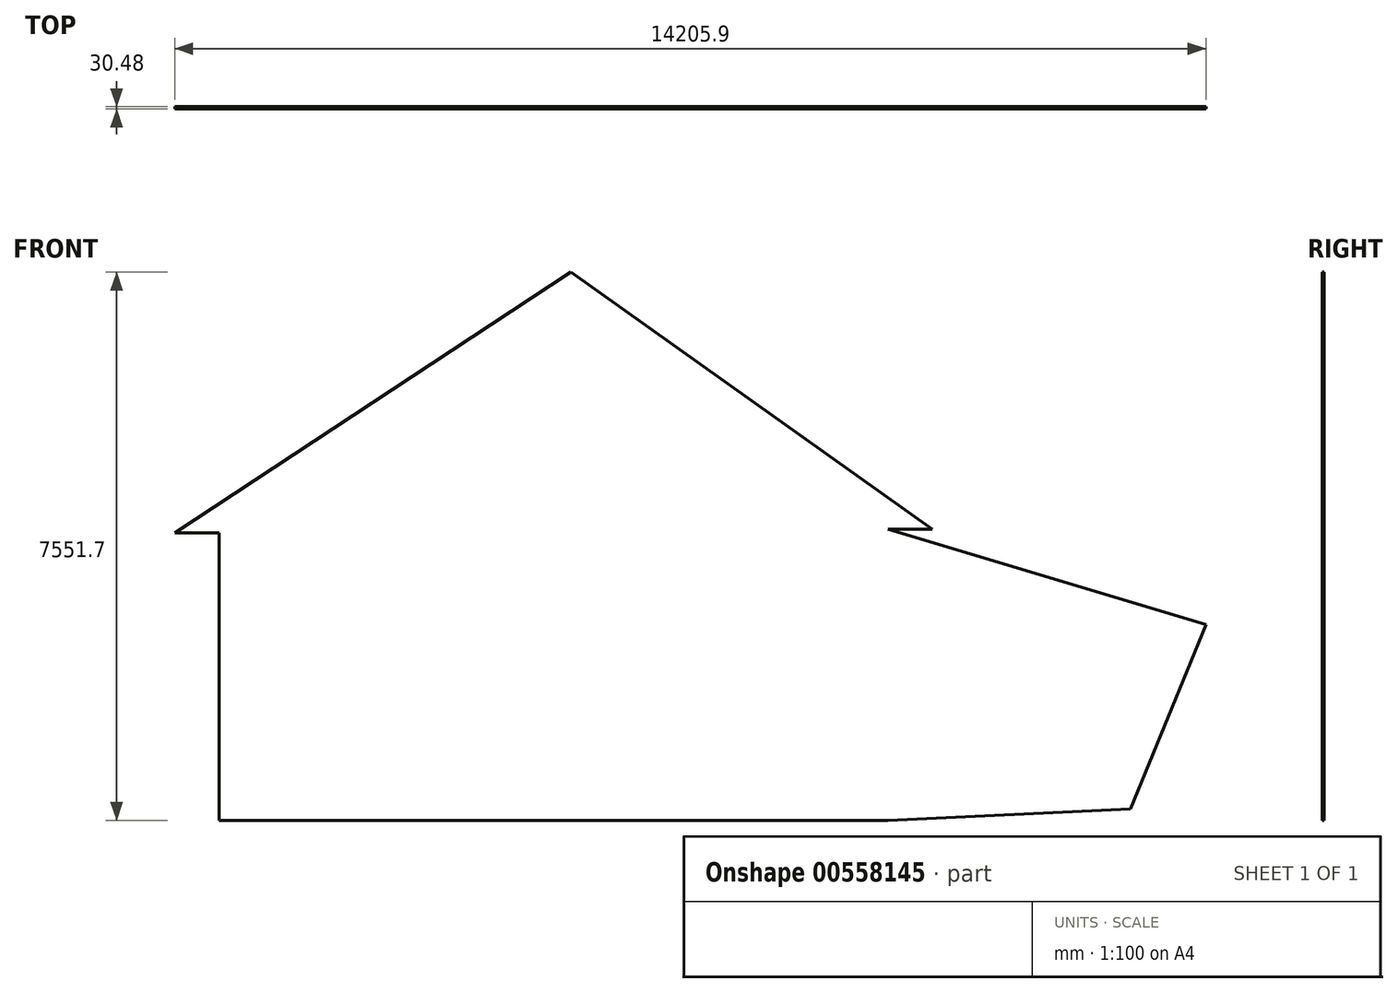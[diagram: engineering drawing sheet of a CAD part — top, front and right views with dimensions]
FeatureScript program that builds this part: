
annotation { "Feature Type Name" : "Feature", "Feature Type Description" : "" }
export const myFeature = defineFeature(function(context is Context, id is Id, definition is map)
    precondition{}
    {
        {
            var Q0;
            Q0=qCreatedBy(makeId("Front.planeOp"),FACE);
            var sketch = newSketch(context, id + "F0", { "sketchPlane" : qUnion([Q0])});
            skLineSegment(sketch, "E0", {"start": v(0, 0) * mm, "end": v(-4572, 0) * mm});
            skLineSegment(sketch, "E1", {"start": v(0, 0) * mm, "end": v(4572, 0) * mm});
            skLineSegment(sketch, "E2", {"start": v(-4572, 0) * mm, "end": v(0, 2750.77) * mm});
            skLineSegment(sketch, "E3", {"start": v(4644.56, 46.62) * mm, "end": v(0, 2750.77) * mm});
            skLineSegment(sketch, "E4", {"start": v(-4572, 0) * mm, "end": v(-4572, -3352.8) * mm});
            skLineSegment(sketch, "E5", {"start": v(4644.56, 46.62) * mm, "end": v(4644.56, -3352.8) * mm});
            skLineSegment(sketch, "E6", {"start": v(4644.56, -3352.8) * mm, "end": v(-4572, -3352.8) * mm});
            skLineSegment(sketch, "E7", {"start": v(-4572, -3352.8) * mm, "end": v(-4572, -3962.4) * mm});
            skLineSegment(sketch, "E8", {"start": v(4644.56, -3352.8) * mm, "end": v(4644.56, -3962.4) * mm});
            skLineSegment(sketch, "E9", {"start": v(-4572, -3962.4) * mm, "end": v(4644.56, -3962.4) * mm});
            skLineSegment(sketch, "E10", {"start": v(-266.42, -1756.14) * mm, "end": v(-266.42, -3352.8) * mm});
            skLineSegment(sketch, "E11", {"start": v(-266.42, -1756.14) * mm, "end": v(821.46, -1756.14) * mm});
            skLineSegment(sketch, "E12", {"start": v(821.46, -1756.14) * mm, "end": v(821.46, -3352.8) * mm});
            skLineSegment(sketch, "E13", {"start": v(-4151.68, -810.66) * mm, "end": v(-4151.68, -1725.06) * mm});
            skLineSegment(sketch, "E14", {"start": v(-4151.68, -1725.06) * mm, "end": v(-2193.5, -1725.06) * mm});
            skLineSegment(sketch, "E15", {"start": v(-2193.5, -1725.06) * mm, "end": v(-2193.5, -854.76) * mm});
            skLineSegment(sketch, "E16", {"start": v(-2193.5, -854.76) * mm, "end": v(-4151.68, -810.66) * mm});
            skLineSegment(sketch, "E17.bottom", {"start": v(1598.5, -1010.17) * mm, "end": v(2748.55, -1010.17) * mm});
            skLineSegment(sketch, "E17.top", {"start": v(1598.5, -1693.97) * mm, "end": v(2748.55, -1693.97) * mm});
            skLineSegment(sketch, "E17.left", {"start": v(1598.5, -1010.17) * mm, "end": v(1598.5, -1693.97) * mm});
            skLineSegment(sketch, "E17.right", {"start": v(2748.55, -1010.17) * mm, "end": v(2748.55, -1693.97) * mm});
            skLineSegment(sketch, "E18", {"start": v(-4572, 0) * mm, "end": v(-5181.6, 0) * mm});
            skLineSegment(sketch, "E19", {"start": v(4644.56, 46.62) * mm, "end": v(5254.16, 46.62) * mm});
            skLineSegment(sketch, "E20", {"start": v(5254.16, 46.62) * mm, "end": v(276.79, 3589.3) * mm});
            skLineSegment(sketch, "E21", {"start": v(-5181.6, 0) * mm, "end": v(276.79, 3589.3) * mm});
            skLineSegment(sketch, "E22", {"start": v(4644.56, 46.62) * mm, "end": v(9024.27, -1265.34) * mm});
            skLineSegment(sketch, "E23", {"start": v(9024.27, -1265.34) * mm, "end": v(7988.12, -3805.33) * mm});
            skLineSegment(sketch, "E24", {"start": v(4644.56, -3962.4) * mm, "end": v(7988.12, -3805.33) * mm});
            skLineSegment(sketch, "E25", {"start": v(4644.56, -3352.8) * mm, "end": v(8172.72, -3352.8) * mm});
            skLineSegment(sketch, "E26.bottom", {"start": v(5859.42, -1676.82) * mm, "end": v(7251.6, -1676.82) * mm});
            skLineSegment(sketch, "E26.top", {"start": v(5859.42, -2893.75) * mm, "end": v(7251.6, -2893.75) * mm});
            skLineSegment(sketch, "E26.left", {"start": v(5859.42, -1676.82) * mm, "end": v(5859.42, -2893.75) * mm});
            skLineSegment(sketch, "E26.right", {"start": v(7251.6, -1676.82) * mm, "end": v(7251.6, -2893.75) * mm});
            skLineSegment(sketch, "E27.bottom", {"start": v(6215.56, -2092.04) * mm, "end": v(6927.84, -2092.04) * mm});
            skLineSegment(sketch, "E27.top", {"start": v(6215.56, -2598.7) * mm, "end": v(6927.84, -2598.7) * mm});
            skLineSegment(sketch, "E27.left", {"start": v(6215.56, -2092.04) * mm, "end": v(6215.56, -2598.7) * mm});
            skLineSegment(sketch, "E27.right", {"start": v(6927.84, -2092.04) * mm, "end": v(6927.84, -2598.7) * mm});
            skLineSegment(sketch, "E28", {"start": v(-777.76, -1261.7) * mm, "end": v(-777.76, -3352.8) * mm});
            skLineSegment(sketch, "E29", {"start": v(-777.76, -1261.7) * mm, "end": v(1261.96, -1261.7) * mm});
            skLineSegment(sketch, "E30", {"start": v(1261.96, -1261.7) * mm, "end": v(1261.96, -3352.8) * mm});
            skLineSegment(sketch, "E31", {"start": v(0, 2750.77) * mm, "end": v(0, 0) * mm, "construction": true});
            skLineSegment(sketch, "E32", {"start": v(276.79, 3589.3) * mm, "end": v(0, 2750.77) * mm, "construction": true});
            skLineSegment(sketch, "E33", {"start": v(4644.56, -556.62) * mm, "end": v(8804.99, -1802.9) * mm});
            skSolve(sketch);
        }
        {
            var Q0;
            Q0=makeQuery(id+"F0.imprint","IMPRINT",FACE,{"disambiguationData":[TD([[makeQuery(id+"F0.imprint","IMPRINT",EDGE,{"derivedFrom":sQuery(id+"F0.wireOp",EDGE,"E2")}),-1.0]])]});
            var Q1;
            {var subQ0=sQuery(id+"F0.wireOp",EDGE,"E10");Q1=makeQuery(id+"F0.imprint","IMPRINT",FACE,{"disambiguationData":[TD([[makeQuery(id+"F0.imprint","IMPRINT",EDGE,{"derivedFrom":subQ0}),1.0]])]});}
            var Q2;
            {var subQ0=sQuery(id+"F0.wireOp",EDGE,"E25");Q2=makeQuery(id+"F0.imprint","IMPRINT",FACE,{"disambiguationData":[TD([[makeQuery(id+"F0.imprint","IMPRINT",EDGE,{"derivedFrom":subQ0}),1.0]])]});}
            var Q3;
            Q3=makeQuery(id+"F0.imprint","IMPRINT",FACE,{"disambiguationData":[TD([[makeQuery(id+"F0.imprint","IMPRINT",EDGE,{"derivedFrom":sQuery(id+"F0.wireOp",EDGE,"E2")}),1.0]])]});
            var Q4;
            {var subQ0=sQuery(id+"F0.wireOp",EDGE,"E22");Q4=makeQuery(id+"F0.imprint","IMPRINT",FACE,{"disambiguationData":[TD([[makeQuery(id+"F0.imprint","IMPRINT",EDGE,{"derivedFrom":subQ0}),-1.0]])]});}
            var Q5;
            {var subQ6=sQuery(id+"F0.wireOp",EDGE,"E7");Q5=makeQuery(id+"F0.imprint","IMPRINT",FACE,{"disambiguationData":[TD([[makeQuery(id+"F0.imprint","IMPRINT",EDGE,{"derivedFrom":subQ6}),1.0]])]});}
            var Q6;
            Q6=makeQuery(id+"F0.imprint","IMPRINT",FACE,{"disambiguationData":[TD([[makeQuery(id+"F0.imprint","IMPRINT",EDGE,{"derivedFrom":sQuery(id+"F0.wireOp",EDGE,"E8")}),1.0]])]});
            var Q7;
            Q7=makeQuery(id+"F0.imprint","IMPRINT",FACE,{"disambiguationData":[TD([[makeQuery(id+"F0.imprint","IMPRINT",EDGE,{"derivedFrom":sQuery(id+"F0.wireOp",EDGE,"E13")}),1.0]])]});
            var Q8;
            {var subQ0=sQuery(id+"F0.wireOp",EDGE,"E10");Q8=makeQuery(id+"F0.imprint","IMPRINT",FACE,{"disambiguationData":[TD([[makeQuery(id+"F0.imprint","IMPRINT",EDGE,{"derivedFrom":subQ0}),-1.0]])]});}
            var Q9;
            Q9=makeQuery(id+"F0.imprint","IMPRINT",FACE,{"disambiguationData":[TD([[makeQuery(id+"F0.imprint","IMPRINT",EDGE,{"derivedFrom":sQuery(id+"F0.wireOp",EDGE,"E27.bottom")}),-1.0]])]});
            var Q10;
            Q10=makeQuery(id+"F0.imprint","IMPRINT",FACE,{"disambiguationData":[TD([[makeQuery(id+"F0.imprint","IMPRINT",EDGE,{"derivedFrom":sQuery(id+"F0.wireOp",EDGE,"E26.bottom")}),-1.0]])]});
            var Q11;
            Q11=makeQuery(id+"F0.imprint","IMPRINT",FACE,{"disambiguationData":[TD([[makeQuery(id+"F0.imprint","IMPRINT",EDGE,{"derivedFrom":sQuery(id+"F0.wireOp",EDGE,"E17.bottom")}),-1.0]])]});
            extrude(context, id + "F1", {"entities" : qUnion([Q0, Q1, Q2, Q3, Q4, Q5, Q6, Q7, Q8, Q9, Q10, Q11]), "depth" : 30.48 * mm, "offsetDistance" : 30.48 * mm});
        }
    });
